# Revit family: 0045109 Sylvania Lighting Fixture OPTIX S 1500x200 2 LINES D-I HO 4K WHT SSH EM
name_source: partatom
category: Lighting Fixtures
revit_build: Autodesk Revit 2018 (Build: 20170223_1515(x64)
units: mm (PartAtom-declared; Revit-internal decimal feet)

## family parameters
Cut with Voids When Loaded = No
Host = Face
Light Source = Yes
OmniClass Number = 23.80.70.00
OmniClass Title = Lighting
Part Type = Normal
Room Calculation Point = No
Round Connector Dimension = Use Diameter
Shared = No

## types (1)
- 0045109 OPTIX S 1500 2L D/I HO 4K WHT SSH EM
    Apparent Load = 44 VA
    Assembly Code = D5020200
    AssetType = Fixed
    ClassificationName = Uniclass2015
    ClassificationValue = EF_70_80
    Color Filter = 16777215
    Cost = 0 $
    Default Elevation = 1219 mm
    Description = OPTIX S 1500x200 2 LINES D/I HO 4000K WHITE SSH EM is a high efficacy low glare luminaire for office and education applications. Direct / Indirect lighting with 80% downlight and 20% uplight ratio for ceiling suspended mounting. Size: 1410x200x45mm. White plastic low glare optics in 2 lines configuration. White RAL9016 fixture body. SylSmart Connected Building capable. 3hr maintained emergency version. 4000K Neutral White LED, CRI>80, chromaticity tolerance of 3-step MacAdam ellipse. Luminous flux 7000lm. Power consumption 48W. Luminaire efficacy 146lm/W. Lumen maintenance of L90B50 = 44000h. UGR<19, Luminance at 65°<3000 Cd/m2, IK07, IP20. Photobiological safety risk group 1. Electrical protection Class I. Glow wire test 850°C.
    Dimming Lamp Color Temperature Shift = <None>
    DocumentationLiterature = http://www.sylvania-lighting.com
    DurationUnit = hours
    ElectricShockClassification = 159
    Emit Shape Visible in Rendering = No
    Emit from Circle Diameter = 610 mm
    ExpectedLife = 50000
    Height = 53 mm  [stored 0.173885 ft]
    IfcExportAs = Class I
    IfcExportType = IfcLightFixtureType
    ImpactProtectionIndex = IfcLightFixtureType
    IngressProtection = IfcLightFixtureType
    InputNominalFrequency = 4000
    InputVoltage = 0
    LampColourRenderingIndex = 16500
    LampColourTemperature = LED
    LampMacAdamStep = 80
    LampNominalLuminous = 4000 K
    Length = 1410 mm  [stored 4.62598 ft]
    LightOutputRatio = LED
    LuminaireType = 0
    ManufacturerName = 159 lm/W
    Material = Feilo Sylvania
    Material_1_FEILO = <By Category>
    Material_2_FEILO = <By Category>
    Material_3_FEILO = <By Category>
    Material_4_FEILO = <By Category>
    Model = OPTIX S 1500x200 2 LINES D/I HO 4K WHT SSH EM
    ModelNumber = 0045109
    ModelReference = OPTIX S 1500x200 2 LINES D/I HO 4K WHT SSH EM
    Name = OPTIX S 1500x200 2 LINES D/I HO 4K WHT SSH EM
    NominalDepth = 0 mm  [stored 0 ft]
    NominalHeight = 0 mm  [stored 0 ft]
    NominalLength = 200 mm  [stored 0.656168 ft]
    Photometric Web File = 0045109EM.ies
    PowerConsumption = Lighting
    PowerFactor = 0
    Tilt Angle = 90.00°
    Type Image = <None>
    TypeName = OPTIX S 1500x200 2 LINES D/I HO 4K WHT SSH EM
    URL = 0.96
    Voltage = 0 V
    WarrantyDescription = http://www.sylvania-lighting.com
    Width = 200 mm  [stored 0.656168 ft]
    spacer centres = 1000 mm  [stored 3.28084 ft]
    spacer height = 8 mm  [stored 0.0262467 ft]

note: [stored X ft] marks values corroborated as IEEE doubles in the binary element streams (Revit-internal decimal feet)

## geometry (parser evidence)
native form markers: Sweep x3
no freeform markers — native parametric forms only
